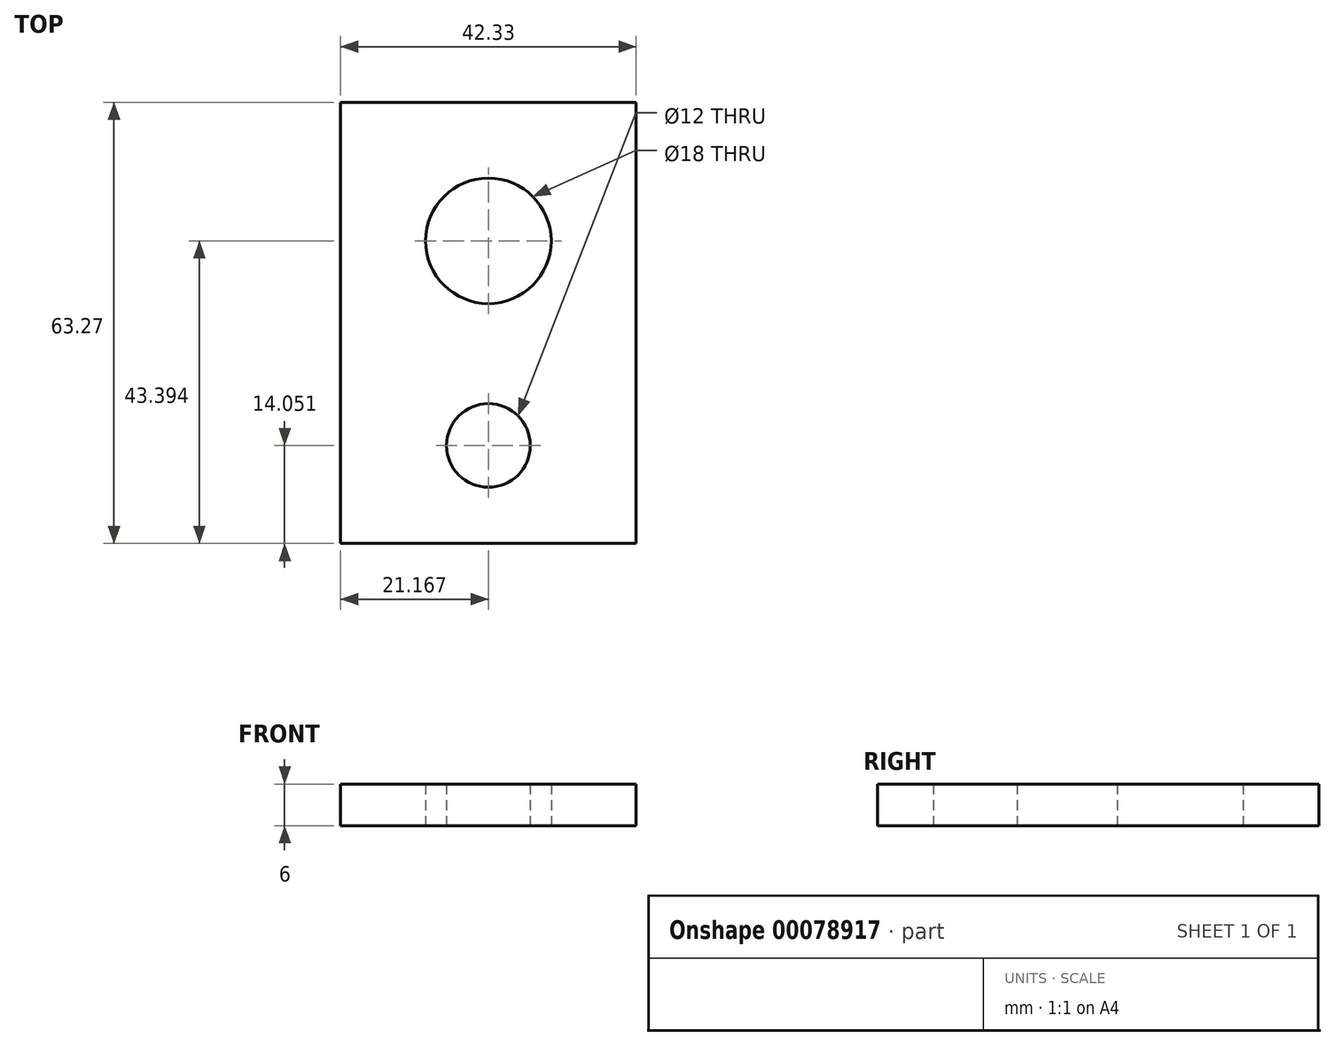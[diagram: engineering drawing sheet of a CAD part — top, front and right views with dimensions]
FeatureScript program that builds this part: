
annotation { "Feature Type Name" : "Feature", "Feature Type Description" : "" }
export const myFeature = defineFeature(function(context is Context, id is Id, definition is map)
    precondition{}
    {
        {
            var Q0;
            Q0=qCreatedBy(makeId("Top.planeOp"),FACE);
            var sketch = newSketch(context, id + "F0", { "sketchPlane" : qUnion([Q0])});
            skLineSegment(sketch, "E0.bottom", {"start": v(0, 0) * mm, "end": v(42.33, 0) * mm});
            skLineSegment(sketch, "E0.top", {"start": v(0, 63.27) * mm, "end": v(42.33, 63.27) * mm});
            skLineSegment(sketch, "E0.left", {"start": v(0, 0) * mm, "end": v(0, 63.27) * mm});
            skLineSegment(sketch, "E0.right", {"start": v(42.33, 0) * mm, "end": v(42.33, 63.27) * mm});
            skLineSegment(sketch, "E1", {"start": v(21.17, 63.27) * mm, "end": v(21.17, 0) * mm, "construction": true});
            skCircle(sketch, "E2", {"center": v(21.17, 14.05) * mm, "radius": 6 * mm});
            skCircle(sketch, "E3", {"center": v(21.17, 43.4) * mm, "radius": 9 * mm});
            skSolve(sketch);
        }
        {
            var Q0;
            Q0 = qSketchRegion(id + "F0", true);
            extrude(context, id + "F1", {"entities" : qUnion([Q0]), "depth" : 6 * mm});
        }
    });
